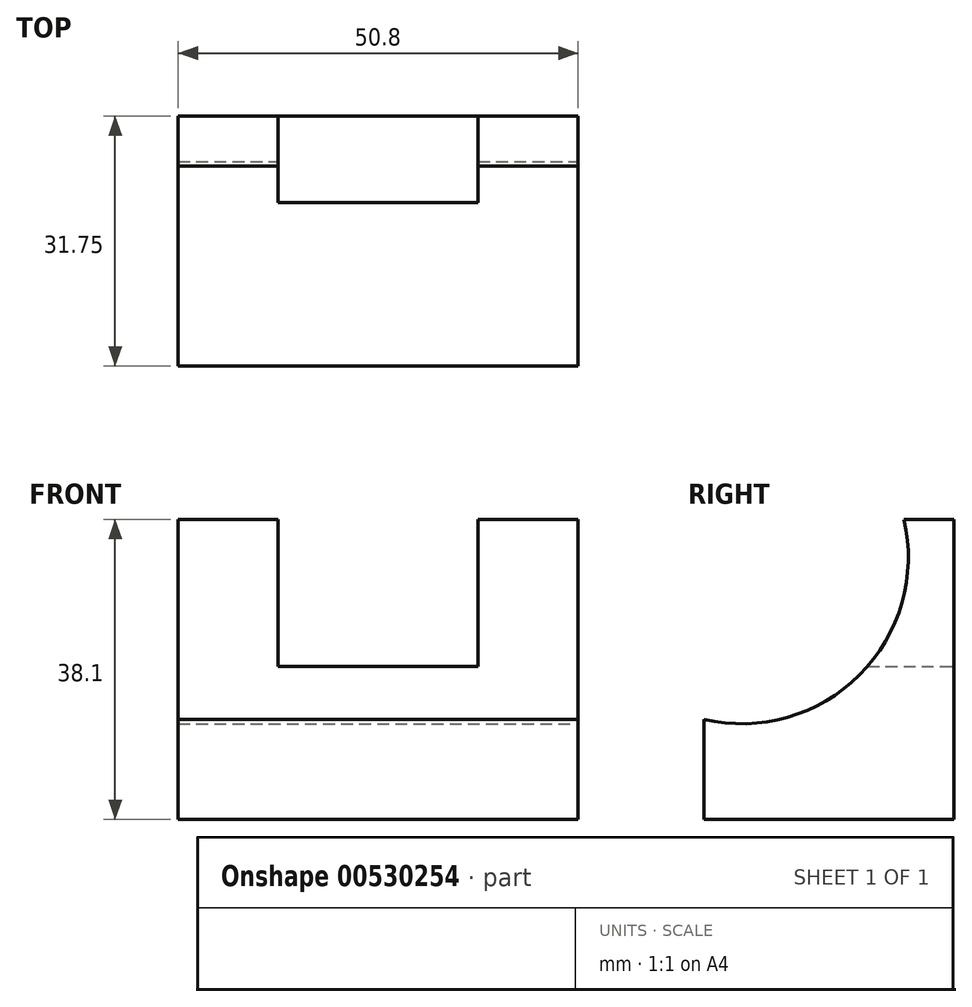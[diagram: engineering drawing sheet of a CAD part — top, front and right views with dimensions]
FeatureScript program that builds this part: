
annotation { "Feature Type Name" : "Feature", "Feature Type Description" : "" }
export const myFeature = defineFeature(function(context is Context, id is Id, definition is map)
    precondition{}
    {
        {
            var Q0;
            Q0=qCreatedBy(makeId("Right.planeOp"),FACE);
            var sketch = newSketch(context, id + "F0", { "sketchPlane" : qUnion([Q0])});
            skLineSegment(sketch, "E0", {"start": v(-59.02, 0) * mm, "end": v(-27.27, 0) * mm});
            skLineSegment(sketch, "E1", {"start": v(-27.27, 0) * mm, "end": v(-27.27, 38.1) * mm});
            skLineSegment(sketch, "E2", {"start": v(-27.27, 38.1) * mm, "end": v(-59.02, 38.1) * mm});
            skLineSegment(sketch, "E3", {"start": v(-59.02, 38.1) * mm, "end": v(-59.02, 0) * mm});
            skSolve(sketch);
        }
        {
            var Q0;
            Q0 = qSketchRegion(id + "F0", true);
            extrude(context, id + "F1", {"entities" : qUnion([Q0]), "depth" : 50.8 * mm, "offsetDistance" : 25.4 * mm});
        }
        {
            var Q0;
            Q0=makeQuery(id+"F1.opExtrude","CAP_FACE",FACE,{"disambiguationData":[OSD([sQuery(id+"F0.wireOp",EDGE,"E0"),sQuery(id+"F0.wireOp",EDGE,"E1"),sQuery(id+"F0.wireOp",EDGE,"E2"),sQuery(id+"F0.wireOp",EDGE,"E3")])],"isStart":false});
            var sketch = newSketch(context, id + "F2", { "sketchPlane" : qUnion([Q0])});
            skArc(sketch, "E4", {"start": v(-59.02, 12.7) * mm, "mid": v(-39.28, 18.35) * mm, "end": v(-33.62, 38.1) * mm});
            skSolve(sketch);
        }
        {
            var Q0;
            Q0 = qSketchRegion(id + "F2", true);
            var Q1;
            {var subQ0=sQuery(id+"F2.wireOp",EDGE,"E4");Q1=makeQuery(id+"F2.imprint","IMPRINT",FACE,{"disambiguationData":[TD([[makeQuery(id+"F2.imprint","IMPRINT",EDGE,{"derivedFrom":subQ0}),1.0]])]});}
            extrude(context, id + "F3", {"entities" : qUnion([Q0, Q1]), "operationType" : NewBodyOperationType.REMOVE, "endBound" : BoundingType.THROUGH_ALL, "oppositeDirection" : true, "depth" : 25.4 * mm, "offsetDistance" : 25.4 * mm});
        }
        {
            var Q0;
            Q0=makeQuery(id+"F1.opExtrude","SWEPT_FACE",FACE,{"disambiguationData":[OSD([sQuery(id+"F0.wireOp",EDGE,"E1")])]});
            var sketch = newSketch(context, id + "F4", { "sketchPlane" : qUnion([Q0])});
            skLineSegment(sketch, "E5", {"start": v(-38.1, 38.1) * mm, "end": v(-38.1, 19.44) * mm});
            skLineSegment(sketch, "E6", {"start": v(-38.1, 19.44) * mm, "end": v(-12.7, 19.44) * mm});
            skLineSegment(sketch, "E7", {"start": v(-12.7, 19.44) * mm, "end": v(-12.7, 38.1) * mm});
            skLineSegment(sketch, "E8", {"start": v(-12.7, 38.1) * mm, "end": v(-38.1, 38.1) * mm});
            skSolve(sketch);
        }
        {
            var Q0;
            Q0 = qSketchRegion(id + "F4", true);
            extrude(context, id + "F5", {"entities" : qUnion([Q0]), "operationType" : NewBodyOperationType.REMOVE, "oppositeDirection" : true, "depth" : 25.4 * mm, "offsetDistance" : 25.4 * mm});
        }
    });
